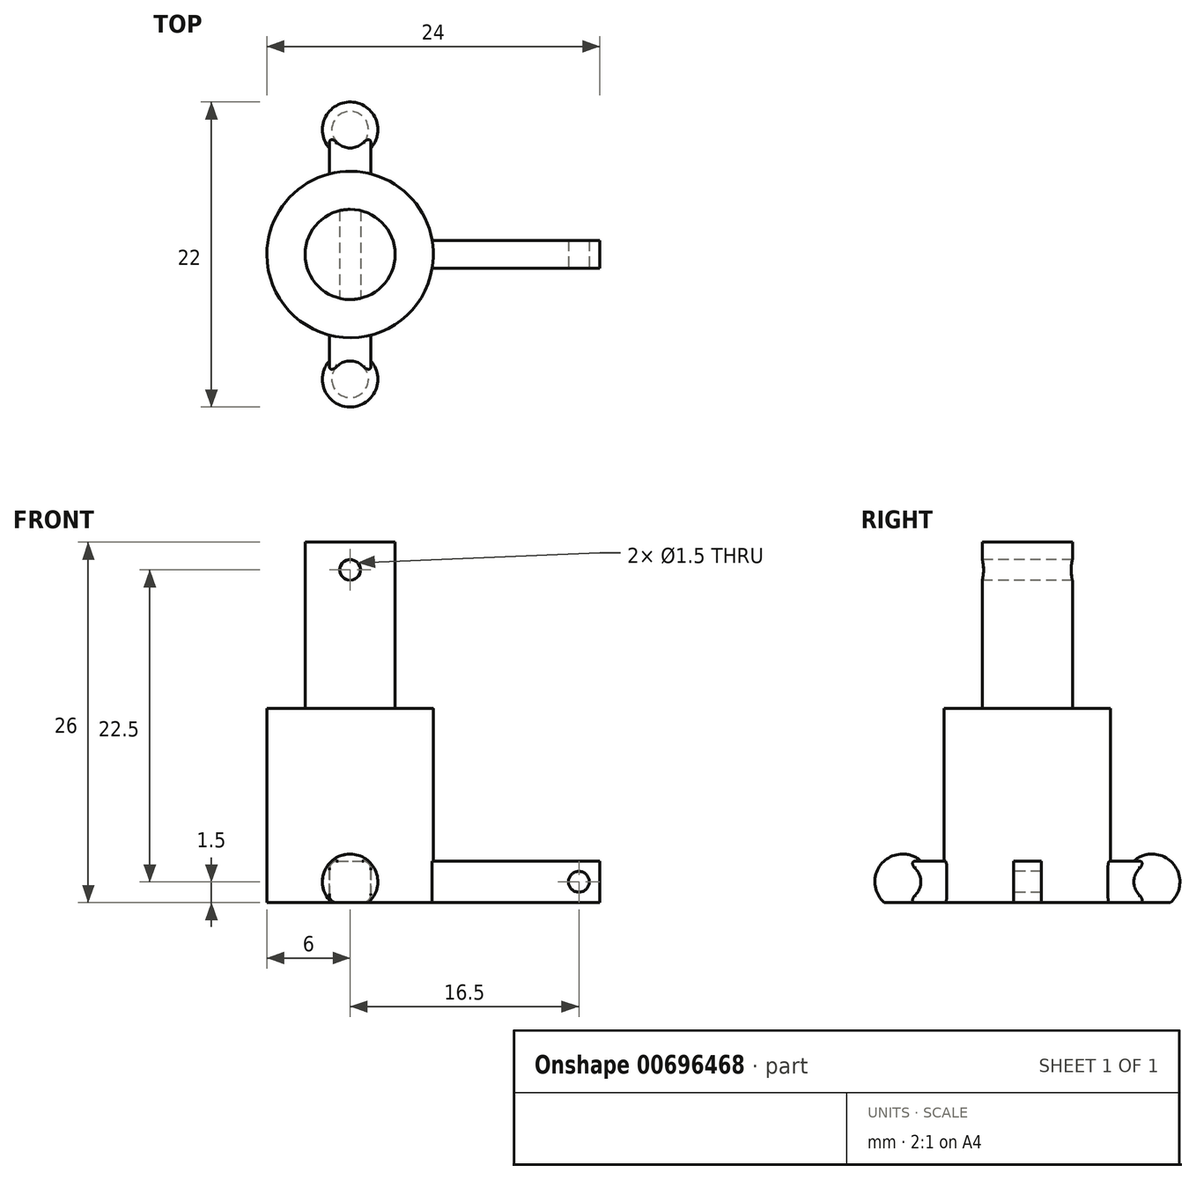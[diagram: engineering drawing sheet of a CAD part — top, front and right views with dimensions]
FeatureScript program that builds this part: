
annotation { "Feature Type Name" : "Feature", "Feature Type Description" : "" }
export const myFeature = defineFeature(function(context is Context, id is Id, definition is map)
    precondition{}
    {
        {
            var Q0;
            Q0=qCreatedBy(makeId("Top.planeOp"),FACE);
            var sketch = newSketch(context, id + "F0", { "sketchPlane" : qUnion([Q0])});
            skCircle(sketch, "E0", {"center": v(0, 0) * mm, "radius": 3.25 * mm});
            skSolve(sketch);
        }
        {
            var Q0;
            Q0 = qSketchRegion(id + "F0", true);
            extrude(context, id + "F1", {"entities" : qUnion([Q0]), "depth" : 12 * mm, "offsetDistance" : 25 * mm});
        }
        {
            var Q0;
            Q0=qCreatedBy(makeId("Front.planeOp"),FACE);
            var sketch = newSketch(context, id + "F2", { "sketchPlane" : qUnion([Q0])});
            skCircle(sketch, "E1", {"center": v(0, 10) * mm, "radius": 0.75 * mm});
            skSolve(sketch);
        }
        {
            var Q0;
            Q0 = qSketchRegion(id + "F2", true);
            extrude(context, id + "F3", {"entities" : qUnion([Q0]), "operationType" : NewBodyOperationType.REMOVE, "endBound" : BoundingType.THROUGH_ALL, "oppositeDirection" : true, "depth" : 25 * mm, "offsetDistance" : 25 * mm, "hasSecondDirection" : true, "secondDirectionBound" : SecondDirectionBoundingType.THROUGH_ALL, "secondDirectionOppositeDirection" : false, "secondDirectionDepth" : 25 * mm});
        }
        {
            var Q0;
            Q0=makeQuery(id+"F1.opExtrude","CAP_FACE",FACE,{"disambiguationData":[OSD([sQuery(id+"F0.wireOp",EDGE,"E0")])],"isStart":true});
            var sketch = newSketch(context, id + "F4", { "sketchPlane" : qUnion([Q0])});
            skCircle(sketch, "E2", {"center": v(0, 0) * mm, "radius": 6 * mm});
            skSolve(sketch);
        }
        {
            var Q0;
            Q0 = qSketchRegion(id + "F4", true);
            extrude(context, id + "F5", {"entities" : qUnion([Q0]), "operationType" : NewBodyOperationType.ADD, "depth" : 14 * mm, "offsetDistance" : 25 * mm});
        }
        {
            var Q0;
            Q0=makeQuery(id+"F5.opExtrude","CAP_FACE",FACE,{"disambiguationData":[OSD([sQuery(id+"F4.wireOp",EDGE,"E2")])],"isStart":false});
            var sketch = newSketch(context, id + "F6", { "sketchPlane" : qUnion([Q0])});
            skLineSegment(sketch, "E3.bottom", {"start": v(1.5, 9) * mm, "end": v(-1.5, 9) * mm});
            skLineSegment(sketch, "E3.top", {"start": v(1.5, -9) * mm, "end": v(-1.5, -9) * mm});
            skLineSegment(sketch, "E3.left", {"start": v(1.5, 9) * mm, "end": v(1.5, -9) * mm});
            skLineSegment(sketch, "E3.right", {"start": v(-1.5, 9) * mm, "end": v(-1.5, -9) * mm});
            skPoint(sketch, "E3.middle", {"position": v(0, 0) * mm});
            skSolve(sketch);
        }
        {
            var Q0;
            Q0 = qSketchRegion(id + "F6", true);
            extrude(context, id + "F7", {"entities" : qUnion([Q0]), "operationType" : NewBodyOperationType.ADD, "oppositeDirection" : true, "depth" : 3 * mm, "offsetDistance" : 25 * mm});
        }
        {
            var Q0;
            Q0=makeQuery(id+"F7.opExtrude","CAP_EDGE",EDGE,{"disambiguationData":[OSD([sQuery(id+"F6.wireOp",EDGE,"E3.bottom")])],"isStart":false});
            var Q1;
            Q1=makeQuery(id+"F7.opExtrude","SWEPT_EDGE",EDGE,{"disambiguationData":[OSD([sQuery(id+"F6.wireOp",EDGE,"E3.bottom"),sQuery(id+"F6.wireOp",EDGE,"E3.left")])]});
            var Q2;
            Q2=makeQuery(id+"F7.opExtrude","CAP_EDGE",EDGE,{"disambiguationData":[OSD([sQuery(id+"F6.wireOp",EDGE,"E3.bottom")])],"isStart":true});
            var Q3;
            Q3=makeQuery(id+"F7.opExtrude","SWEPT_EDGE",EDGE,{"disambiguationData":[OSD([sQuery(id+"F6.wireOp",EDGE,"E3.bottom"),sQuery(id+"F6.wireOp",EDGE,"E3.right")])]});
            var Q4;
            Q4=makeQuery(id+"F7.opExtrude","SWEPT_EDGE",EDGE,{"disambiguationData":[OSD([sQuery(id+"F6.wireOp",EDGE,"E3.top"),sQuery(id+"F6.wireOp",EDGE,"E3.left")])]});
            var Q5;
            Q5=makeQuery(id+"F7.opExtrude","CAP_EDGE",EDGE,{"disambiguationData":[OSD([sQuery(id+"F6.wireOp",EDGE,"E3.top")])],"isStart":false});
            var Q6;
            Q6=makeQuery(id+"F7.opExtrude","SWEPT_EDGE",EDGE,{"disambiguationData":[OSD([sQuery(id+"F6.wireOp",EDGE,"E3.top"),sQuery(id+"F6.wireOp",EDGE,"E3.right")])]});
            var Q7;
            Q7=makeQuery(id+"F7.opExtrude","CAP_EDGE",EDGE,{"disambiguationData":[OSD([sQuery(id+"F6.wireOp",EDGE,"E3.top")])],"isStart":true});
            fillet(context, id + "F8", {"entities" : qUnion([Q0, Q1, Q2, Q3, Q4, Q5, Q6, Q7]), "radius" : 1 * mm, "tangentPropagation" : true, "allowEdgeOverflow" : false});
        }
        {
            var Q0;
            Q0=makeQuery(id+"F7.opExtrude","SWEPT_FACE",FACE,{"disambiguationData":[OSD([sQuery(id+"F6.wireOp",EDGE,"E3.bottom")])]});
            var sketch = newSketch(context, id + "F9", { "sketchPlane" : qUnion([Q0])});
            skArc(sketch, "E4", {"start": v(0, -14.5) * mm, "mid": v(2, -12.5) * mm, "end": v(0, -10.5) * mm});
            skLineSegment(sketch, "E5", {"start": v(0, -12) * mm, "end": v(0, -13) * mm, "construction": true});
            skLineSegment(sketch, "E6", {"start": v(0, -13) * mm, "end": v(-0.5, -12.5) * mm, "construction": true});
            skLineSegment(sketch, "E7", {"start": v(-0.5, -12.5) * mm, "end": v(0.5, -12.5) * mm, "construction": true});
            skLineSegment(sketch, "E8", {"start": v(0, -10.5) * mm, "end": v(0, -14.5) * mm});
            skSolve(sketch);
        }
        {
            var Q0;
            Q0 = qSketchRegion(id + "F9", true);
            var Q1;
            Q1=sQuery(id+"F9.wireOp",EDGE,"E8");
            revolve(context, id + "F10", {"operationType" : NewBodyOperationType.ADD, "surfaceOperationType" : NewSurfaceOperationType.NEW, "entities" : qUnion([Q0]), "axis" : qUnion([Q1]), "revolveType" : RevolveType.ONE_DIRECTION, "angle" : 360 * degree});
        }
        {
            var Q0;
            {var subQ0=sQuery(id+"F6.wireOp",EDGE,"E3.bottom");var subQ1=sQuery(id+"F6.wireOp",EDGE,"E3.left");Q0=makeQuery(id+"F7.boolean.opBoolean","SPLIT",EDGE,{"disambiguationData":[TD([makeQuery(id+"F7.opExtrude","SWEPT_FACE",FACE,{"disambiguationData":[OSD([subQ0])]})])],"derivedFrom":makeQuery(id+"F7.opExtrude","CAP_EDGE",EDGE,{"disambiguationData":[OSD([subQ1])],"isStart":false})});}
            var Q1;
            {var subQ0=sQuery(id+"F6.wireOp",EDGE,"E3.bottom");var subQ1=sQuery(id+"F6.wireOp",EDGE,"E3.right");Q1=makeQuery(id+"F7.boolean.opBoolean","SPLIT",EDGE,{"disambiguationData":[TD([makeQuery(id+"F7.opExtrude","SWEPT_FACE",FACE,{"disambiguationData":[OSD([subQ0])]})])],"derivedFrom":makeQuery(id+"F7.opExtrude","CAP_EDGE",EDGE,{"disambiguationData":[OSD([subQ1])],"isStart":false})});}
            var Q2;
            {var subQ0=sQuery(id+"F6.wireOp",EDGE,"E3.bottom");Q2=makeQuery(id+"F8.opFillet","BLEND_EDGE",EDGE,{"blendedFrom":[makeQuery(id+"F7.opExtrude","SWEPT_EDGE",EDGE,{"disambiguationData":[OSD([subQ0,sQuery(id+"F6.wireOp",EDGE,"E3.right")])]}),makeQuery(id+"F7.opExtrude","CAP_EDGE",EDGE,{"disambiguationData":[OSD([subQ0])],"isStart":false})],"blendedInto":[]});}
            var Q3;
            {var subQ0=sQuery(id+"F6.wireOp",EDGE,"E3.bottom");Q3=makeQuery(id+"F8.opFillet","BLEND_EDGE",EDGE,{"blendedFrom":[makeQuery(id+"F7.opExtrude","SWEPT_EDGE",EDGE,{"disambiguationData":[OSD([subQ0,sQuery(id+"F6.wireOp",EDGE,"E3.left")])]}),makeQuery(id+"F7.opExtrude","CAP_EDGE",EDGE,{"disambiguationData":[OSD([subQ0])],"isStart":false})],"blendedInto":[]});}
            var Q4;
            {var subQ0=sQuery(id+"F6.wireOp",EDGE,"E3.bottom");var subQ2=sQuery(id+"F6.wireOp",EDGE,"E3.left");Q4=makeQuery(id+"F7.boolean.opBoolean","SPLIT",EDGE,{"disambiguationData":[TD([makeQuery(id+"F7.opExtrude","SWEPT_FACE",FACE,{"disambiguationData":[OSD([subQ0])]})])],"derivedFrom":makeQuery(id+"F7.opExtrude","CAP_EDGE",EDGE,{"disambiguationData":[OSD([subQ2])],"isStart":true})});}
            var Q5;
            {var subQ0=sQuery(id+"F6.wireOp",EDGE,"E3.bottom");Q5=makeQuery(id+"F8.opFillet","BLEND_EDGE",EDGE,{"blendedFrom":[makeQuery(id+"F7.opExtrude","SWEPT_EDGE",EDGE,{"disambiguationData":[OSD([subQ0,sQuery(id+"F6.wireOp",EDGE,"E3.left")])]}),makeQuery(id+"F7.opExtrude","CAP_EDGE",EDGE,{"disambiguationData":[OSD([subQ0])],"isStart":true})],"blendedInto":[]});}
            var Q6;
            {var subQ0=sQuery(id+"F6.wireOp",EDGE,"E3.bottom");var subQ2=sQuery(id+"F6.wireOp",EDGE,"E3.right");Q6=makeQuery(id+"F7.boolean.opBoolean","SPLIT",EDGE,{"disambiguationData":[TD([makeQuery(id+"F7.opExtrude","SWEPT_FACE",FACE,{"disambiguationData":[OSD([subQ0])]})])],"derivedFrom":makeQuery(id+"F7.opExtrude","CAP_EDGE",EDGE,{"disambiguationData":[OSD([subQ2])],"isStart":true})});}
            var Q7;
            {var subQ0=sQuery(id+"F6.wireOp",EDGE,"E3.bottom");Q7=makeQuery(id+"F8.opFillet","BLEND_EDGE",EDGE,{"blendedFrom":[makeQuery(id+"F7.opExtrude","SWEPT_EDGE",EDGE,{"disambiguationData":[OSD([subQ0,sQuery(id+"F6.wireOp",EDGE,"E3.right")])]}),makeQuery(id+"F7.opExtrude","CAP_EDGE",EDGE,{"disambiguationData":[OSD([subQ0])],"isStart":true})],"blendedInto":[]});}
            var Q8;
            {var subQ0=sQuery(id+"F6.wireOp",EDGE,"E3.right");var subQ1=sQuery(id+"F6.wireOp",EDGE,"E3.top");Q8=makeQuery(id+"F7.boolean.opBoolean","SPLIT",EDGE,{"disambiguationData":[TD([makeQuery(id+"F7.opExtrude","SWEPT_FACE",FACE,{"disambiguationData":[OSD([subQ1])]})])],"derivedFrom":makeQuery(id+"F7.opExtrude","CAP_EDGE",EDGE,{"disambiguationData":[OSD([subQ0])],"isStart":false})});}
            var Q9;
            {var subQ0=sQuery(id+"F6.wireOp",EDGE,"E3.top");Q9=makeQuery(id+"F8.opFillet","BLEND_EDGE",EDGE,{"blendedFrom":[makeQuery(id+"F7.opExtrude","SWEPT_EDGE",EDGE,{"disambiguationData":[OSD([subQ0,sQuery(id+"F6.wireOp",EDGE,"E3.right")])]}),makeQuery(id+"F7.opExtrude","CAP_EDGE",EDGE,{"disambiguationData":[OSD([subQ0])],"isStart":false})],"blendedInto":[]});}
            var Q10;
            {var subQ0=sQuery(id+"F6.wireOp",EDGE,"E3.left");var subQ1=sQuery(id+"F6.wireOp",EDGE,"E3.top");Q10=makeQuery(id+"F7.boolean.opBoolean","SPLIT",EDGE,{"disambiguationData":[TD([makeQuery(id+"F7.opExtrude","SWEPT_FACE",FACE,{"disambiguationData":[OSD([subQ1])]})])],"derivedFrom":makeQuery(id+"F7.opExtrude","CAP_EDGE",EDGE,{"disambiguationData":[OSD([subQ0])],"isStart":false})});}
            var Q11;
            {var subQ0=sQuery(id+"F6.wireOp",EDGE,"E3.top");Q11=makeQuery(id+"F8.opFillet","BLEND_EDGE",EDGE,{"blendedFrom":[makeQuery(id+"F7.opExtrude","SWEPT_EDGE",EDGE,{"disambiguationData":[OSD([subQ0,sQuery(id+"F6.wireOp",EDGE,"E3.left")])]}),makeQuery(id+"F7.opExtrude","CAP_EDGE",EDGE,{"disambiguationData":[OSD([subQ0])],"isStart":false})],"blendedInto":[]});}
            var Q12;
            {var subQ0=sQuery(id+"F6.wireOp",EDGE,"E3.top");var subQ2=sQuery(id+"F6.wireOp",EDGE,"E3.right");Q12=makeQuery(id+"F7.boolean.opBoolean","SPLIT",EDGE,{"disambiguationData":[TD([makeQuery(id+"F7.opExtrude","SWEPT_FACE",FACE,{"disambiguationData":[OSD([subQ0])]})])],"derivedFrom":makeQuery(id+"F7.opExtrude","CAP_EDGE",EDGE,{"disambiguationData":[OSD([subQ2])],"isStart":true})});}
            var Q13;
            {var subQ0=sQuery(id+"F6.wireOp",EDGE,"E3.top");Q13=makeQuery(id+"F8.opFillet","BLEND_EDGE",EDGE,{"blendedFrom":[makeQuery(id+"F7.opExtrude","SWEPT_EDGE",EDGE,{"disambiguationData":[OSD([subQ0,sQuery(id+"F6.wireOp",EDGE,"E3.right")])]}),makeQuery(id+"F7.opExtrude","CAP_EDGE",EDGE,{"disambiguationData":[OSD([subQ0])],"isStart":true})],"blendedInto":[]});}
            var Q14;
            {var subQ0=sQuery(id+"F6.wireOp",EDGE,"E3.top");var subQ2=sQuery(id+"F6.wireOp",EDGE,"E3.left");Q14=makeQuery(id+"F7.boolean.opBoolean","SPLIT",EDGE,{"disambiguationData":[TD([makeQuery(id+"F7.opExtrude","SWEPT_FACE",FACE,{"disambiguationData":[OSD([subQ0])]})])],"derivedFrom":makeQuery(id+"F7.opExtrude","CAP_EDGE",EDGE,{"disambiguationData":[OSD([subQ2])],"isStart":true})});}
            var Q15;
            {var subQ0=sQuery(id+"F6.wireOp",EDGE,"E3.top");Q15=makeQuery(id+"F8.opFillet","BLEND_EDGE",EDGE,{"blendedFrom":[makeQuery(id+"F7.opExtrude","SWEPT_EDGE",EDGE,{"disambiguationData":[OSD([subQ0,sQuery(id+"F6.wireOp",EDGE,"E3.left")])]}),makeQuery(id+"F7.opExtrude","CAP_EDGE",EDGE,{"disambiguationData":[OSD([subQ0])],"isStart":true})],"blendedInto":[]});}
            fillet(context, id + "F11", {"entities" : qUnion([Q0, Q1, Q2, Q3, Q4, Q5, Q6, Q7, Q8, Q9, Q10, Q11, Q12, Q13, Q14, Q15]), "radius" : .5 * mm, "tangentPropagation" : true, "allowEdgeOverflow" : false});
        }
        {
            var Q0;
            Q0=makeQuery(id+"F7.opExtrude","SWEPT_FACE",FACE,{"disambiguationData":[OSD([sQuery(id+"F6.wireOp",EDGE,"E3.top")])]});
            var sketch = newSketch(context, id + "F12", { "sketchPlane" : qUnion([Q0])});
            skLineSegment(sketch, "E9", {"start": v(0, -12) * mm, "end": v(0, -13) * mm, "construction": true});
            skLineSegment(sketch, "E10", {"start": v(-0.5, -12.5) * mm, "end": v(0.5, -12.5) * mm, "construction": true});
            skArc(sketch, "E11", {"start": v(0, -14.5) * mm, "mid": v(2, -12.5) * mm, "end": v(0, -10.5) * mm});
            skLineSegment(sketch, "E12", {"start": v(0, -10.5) * mm, "end": v(0, -14.5) * mm});
            skSolve(sketch);
        }
        {
            var Q0;
            Q0 = qSketchRegion(id + "F12", true);
            var Q1;
            Q1=sQuery(id+"F12.wireOp",EDGE,"E12");
            revolve(context, id + "F13", {"operationType" : NewBodyOperationType.ADD, "surfaceOperationType" : NewSurfaceOperationType.NEW, "entities" : qUnion([Q0]), "axis" : qUnion([Q1]), "revolveType" : RevolveType.FULL});
        }
        {
            var Q0;
            Q0=qCreatedBy(makeId("Right.planeOp"),FACE);
            var sketch = newSketch(context, id + "F14", { "sketchPlane" : qUnion([Q0])});
            skLineSegment(sketch, "E13.bottom", {"start": v(-1, -11) * mm, "end": v(1, -11) * mm});
            skLineSegment(sketch, "E13.top", {"start": v(-1, -14) * mm, "end": v(1, -14) * mm});
            skLineSegment(sketch, "E13.left", {"start": v(-1, -11) * mm, "end": v(-1, -14) * mm});
            skLineSegment(sketch, "E13.right", {"start": v(1, -11) * mm, "end": v(1, -14) * mm});
            skPoint(sketch, "E13.middle", {"position": v(0, -12.5) * mm});
            skSolve(sketch);
        }
        {
            var Q0;
            Q0 = qSketchRegion(id + "F14", true);
            extrude(context, id + "F15", {"entities" : qUnion([Q0]), "operationType" : NewBodyOperationType.ADD, "depth" : 18 * mm, "offsetDistance" : 25 * mm});
        }
        {
            var Q0;
            Q0=makeQuery(id+"F15.opExtrude","SWEPT_FACE",FACE,{"disambiguationData":[OSD([sQuery(id+"F14.wireOp",EDGE,"E13.left")])]});
            var sketch = newSketch(context, id + "F16", { "sketchPlane" : qUnion([Q0])});
            skCircle(sketch, "E14", {"center": v(16.5, -12.5) * mm, "radius": 0.75 * mm});
            skSolve(sketch);
        }
        {
            var Q0;
            Q0 = qSketchRegion(id + "F16", true);
            extrude(context, id + "F17", {"entities" : qUnion([Q0]), "operationType" : NewBodyOperationType.REMOVE, "endBound" : BoundingType.THROUGH_ALL, "oppositeDirection" : true, "depth" : 25 * mm, "offsetDistance" : 25 * mm});
        }
        {
            var Q0;
            Q0=makeQuery(id+"F15.boolean.opBoolean","MERGE",FACE,{"derivedFrom":[makeQuery(id+"F7.boolean.opBoolean","MERGE",FACE,{"derivedFrom":[makeQuery(id+"F5.opExtrude","CAP_FACE",FACE,{"disambiguationData":[OSD([sQuery(id+"F4.wireOp",EDGE,"E2")])],"isStart":false}),makeQuery(id+"F7.opExtrude","CAP_FACE",FACE,{"disambiguationData":[OSD([sQuery(id+"F6.wireOp",EDGE,"E3.bottom"),sQuery(id+"F6.wireOp",EDGE,"E3.top"),sQuery(id+"F6.wireOp",EDGE,"E3.left"),sQuery(id+"F6.wireOp",EDGE,"E3.right")])],"isStart":true})]}),makeQuery(id+"F15.opExtrude","SWEPT_FACE",FACE,{"disambiguationData":[OSD([sQuery(id+"F14.wireOp",EDGE,"E13.top")])]})]});
            var sketch = newSketch(context, id + "F18", { "sketchPlane" : qUnion([Q0])});
            skLineSegment(sketch, "E15.bottom", {"start": v(-5.8, 14.82) * mm, "end": v(5.8, 14.82) * mm});
            skLineSegment(sketch, "E15.top", {"start": v(-5.8, -14.82) * mm, "end": v(5.8, -14.82) * mm});
            skLineSegment(sketch, "E15.left", {"start": v(-5.8, 14.82) * mm, "end": v(-5.8, -14.82) * mm});
            skLineSegment(sketch, "E15.right", {"start": v(5.8, 14.82) * mm, "end": v(5.8, -14.82) * mm});
            skPoint(sketch, "E15.middle", {"position": v(0, 0) * mm});
            skSolve(sketch);
        }
        {
            var Q0;
            Q0 = qSketchRegion(id + "F18", true);
            extrude(context, id + "F19", {"entities" : qUnion([Q0]), "operationType" : NewBodyOperationType.REMOVE, "depth" : 25 * mm, "offsetDistance" : 25 * mm});
        }
    });
